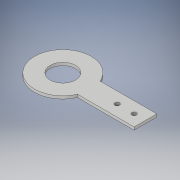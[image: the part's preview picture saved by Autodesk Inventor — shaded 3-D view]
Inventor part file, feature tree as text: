
AUTODESK INVENTOR PART (.ipt)
format: ipt  version: 2019 (Build 230136000, 136)  size: 111,616 bytes
history: native  units: in
note: dims shown in document units (in); Inventor stores cm internally (conversion verified against a paired STEP export)
features: extrude x1, sketch x1
ambient origin geometry x8: Origin, YZ Plane, XZ Plane, XY Plane, X Axis, Y Axis, Z Axis, Center Point
bodies: Solid1 (feature_tree)
feature tree (2):
  extrude  "Extrusion1"  Depth=0.125in
  sketch  "Sketch1"  dims[d6=0.75in d7=0.2031in d8=0.2031in d9=1.125in d10=0.125in d11=0.0in d13=2.5in d14=2.5in d15=0.5in]
